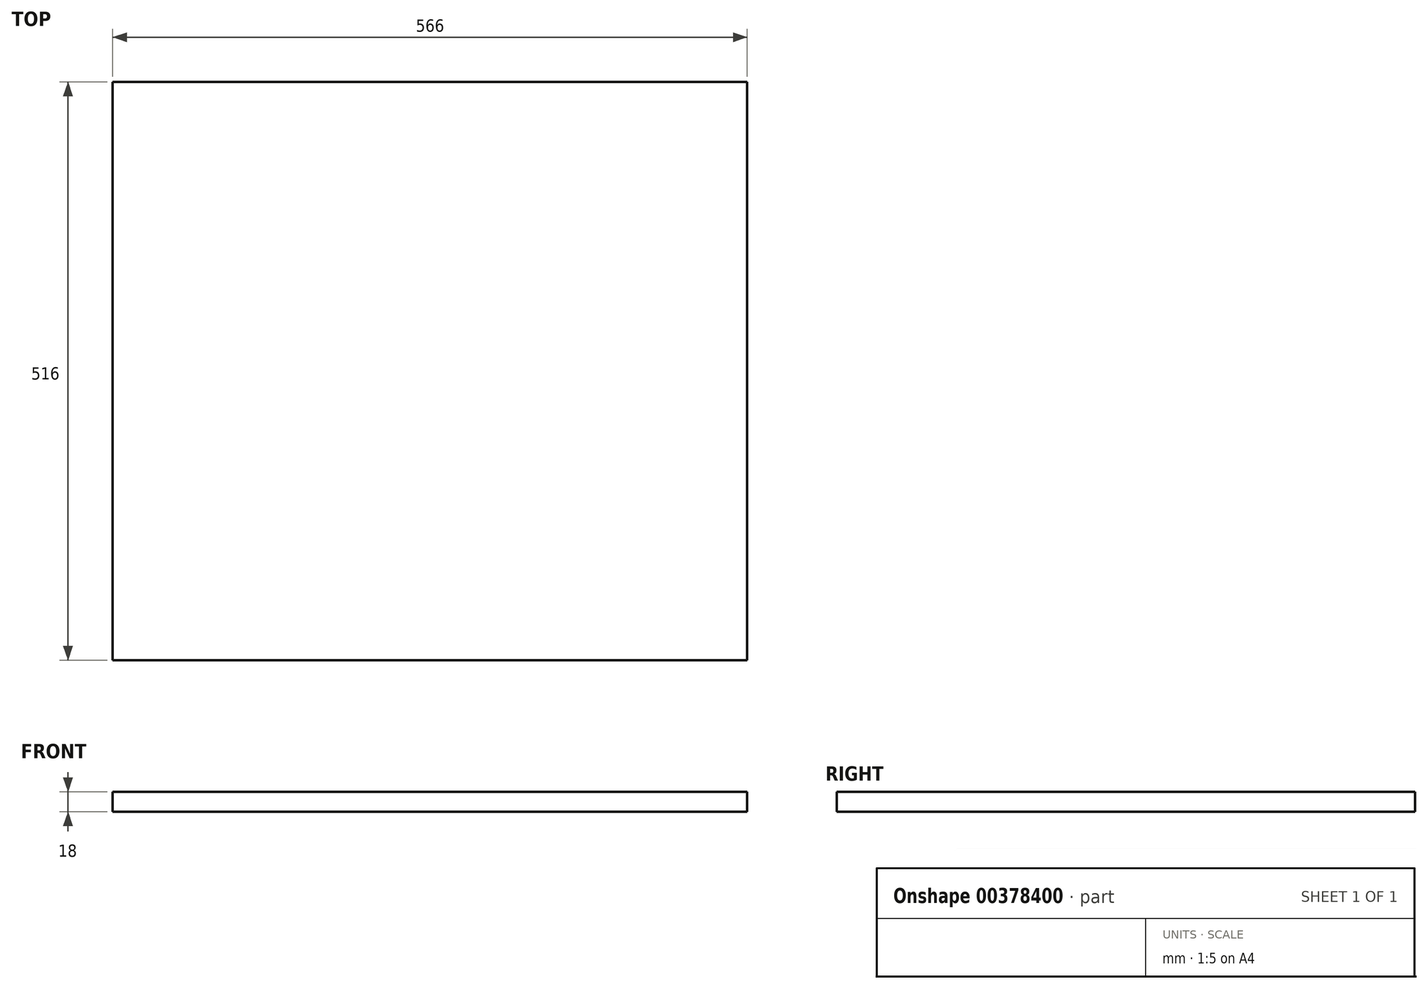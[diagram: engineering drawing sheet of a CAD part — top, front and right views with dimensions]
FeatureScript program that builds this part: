
annotation { "Feature Type Name" : "Feature", "Feature Type Description" : "" }
export const myFeature = defineFeature(function(context is Context, id is Id, definition is map)
    precondition{}
    {
        {
            var Q0;
            Q0=qCreatedBy(makeId("Top.planeOp"),FACE);
            var sketch = newSketch(context, id + "F0", { "sketchPlane" : qUnion([Q0])});
            skLineSegment(sketch, "E0.bottom", {"start": v(283, 258) * mm, "end": v(-283, 258) * mm});
            skLineSegment(sketch, "E0.top", {"start": v(283, -258) * mm, "end": v(-283, -258) * mm});
            skLineSegment(sketch, "E0.left", {"start": v(283, 258) * mm, "end": v(283, -258) * mm});
            skLineSegment(sketch, "E0.right", {"start": v(-283, 258) * mm, "end": v(-283, -258) * mm});
            skPoint(sketch, "E0.middle", {"position": v(0, 0) * mm});
            skSolve(sketch);
        }
        {
            var Q0;
            Q0 = qSketchRegion(id + "F0", true);
            extrude(context, id + "F1", {"entities" : qUnion([Q0]), "depth" : 18 * mm});
        }
    });
